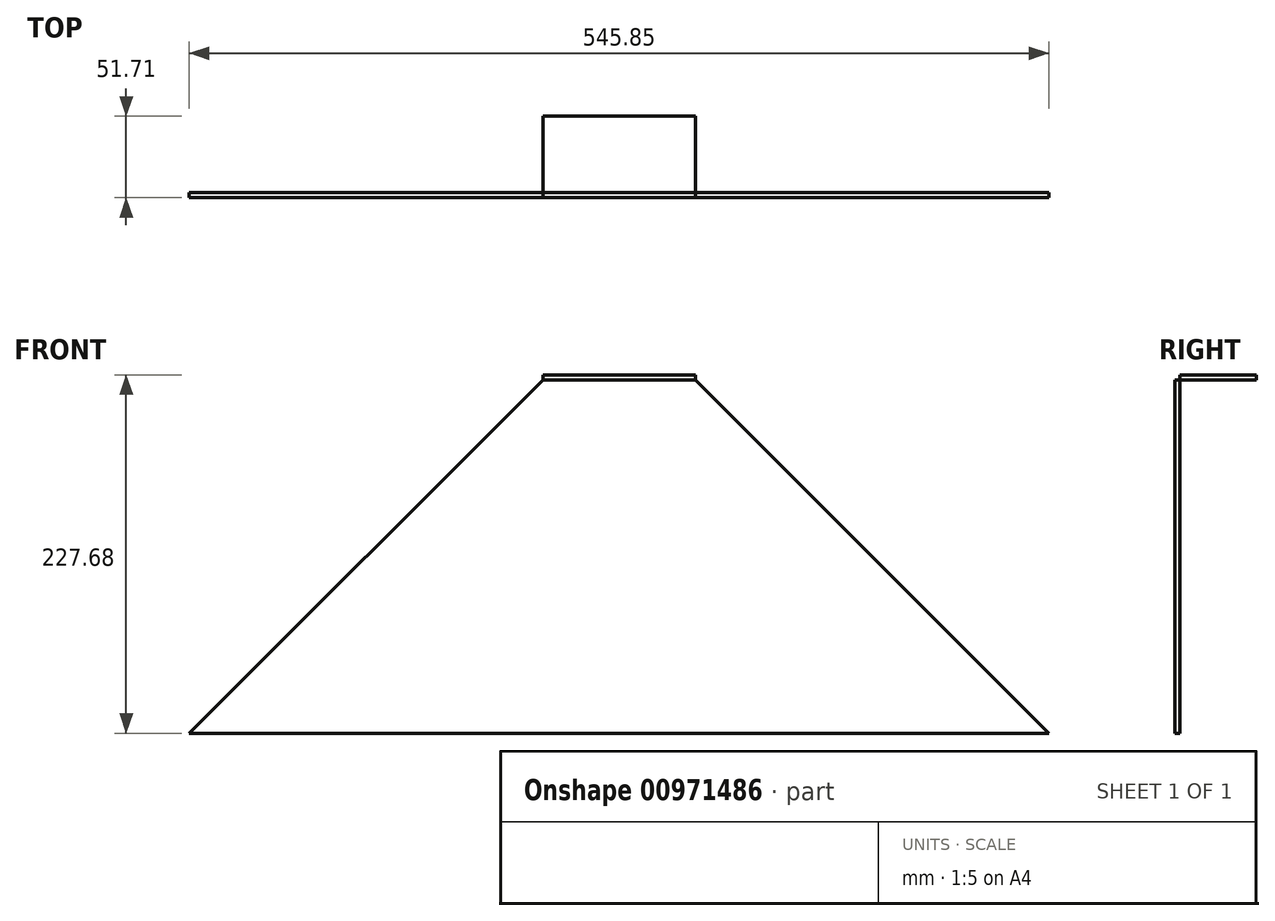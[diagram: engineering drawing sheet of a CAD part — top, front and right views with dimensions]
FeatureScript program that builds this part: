
annotation { "Feature Type Name" : "Feature", "Feature Type Description" : "" }
export const myFeature = defineFeature(function(context is Context, id is Id, definition is map)
    precondition{}
    {
        {
            var Q0;
            Q0=qCreatedBy(makeId("Top.planeOp"),FACE);
            var sketch = newSketch(context, id + "F0", { "sketchPlane" : qUnion([Q0])});
            skLineSegment(sketch, "E0.bottom", {"start": v(-30.34, 48.54) * mm, "end": v(66.49, 48.54) * mm});
            skLineSegment(sketch, "E0.top", {"start": v(-30.34, 0) * mm, "end": v(66.49, 0) * mm});
            skLineSegment(sketch, "E0.left", {"start": v(-30.34, 48.54) * mm, "end": v(-30.34, 0) * mm});
            skLineSegment(sketch, "E0.right", {"start": v(66.49, 48.54) * mm, "end": v(66.49, 0) * mm});
            skSolve(sketch);
        }
        {
            var Q0;
            Q0=qCreatedBy(makeId("Front.planeOp"),FACE);
            var sketch = newSketch(context, id + "F1", { "sketchPlane" : qUnion([Q0])});
            skLineSegment(sketch, "E1", {"start": v(-30.34, 0) * mm, "end": v(-254.85, -224.51) * mm});
            skLineSegment(sketch, "E2", {"start": v(-254.85, -224.51) * mm, "end": v(291, -224.51) * mm});
            skLineSegment(sketch, "E3", {"start": v(291, -224.51) * mm, "end": v(66.49, 0) * mm});
            skLineSegment(sketch, "E4", {"start": v(-30.34, 0) * mm, "end": v(66.49, 0) * mm});
            skSolve(sketch);
        }
        {
            var Q0;
            Q0=makeQuery(id+"F1.imprint","IMPRINT",FACE,{"disambiguationData":[TD([[makeQuery(id+"F1.imprint","IMPRINT",EDGE,{"derivedFrom":sQuery(id+"F1.wireOp",EDGE,"E1")}),1.0]])]});
            extrude(context, id + "F2", {"entities" : qUnion([Q0]), "depth" : 3.17 * mm, "offsetDistance" : 25.4 * mm});
        }
        {
            var Q0;
            Q0=makeQuery(id+"F0.imprint","IMPRINT",FACE,{"disambiguationData":[TD([[makeQuery(id+"F0.imprint","IMPRINT",EDGE,{"derivedFrom":sQuery(id+"F0.wireOp",EDGE,"E0.bottom")}),-1.0]])]});
            extrude(context, id + "F3", {"entities" : qUnion([Q0]), "depth" : 3.17 * mm, "offsetDistance" : 25.4 * mm});
        }
    });
